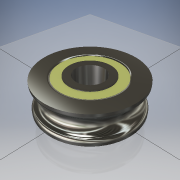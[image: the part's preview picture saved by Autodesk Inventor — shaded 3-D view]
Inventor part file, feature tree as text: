
AUTODESK INVENTOR PART (.ipt)
format: ipt  version: 2016 SP1 (Build 200210100, 210)  size: 190,464 bytes
history: native  units: mm
features: other x3, sketch x2, plane x1
ambient origin geometry x8: Origin, YZ Plane, XZ Plane, XY Plane, X Axis, Y Axis, Z Axis, Center Point
bodies: Solid1 (feature_tree)
feature tree (6):
  other  "idler bearing.ipt"
  other  "Solid1::idler bearing.ipt"
  other  "TaggingFeature1"
  sketch  "Sketch1"  dims[d0=10.0mm]
  sketch  "Sketch2"
  plane  "Work Plane1"
